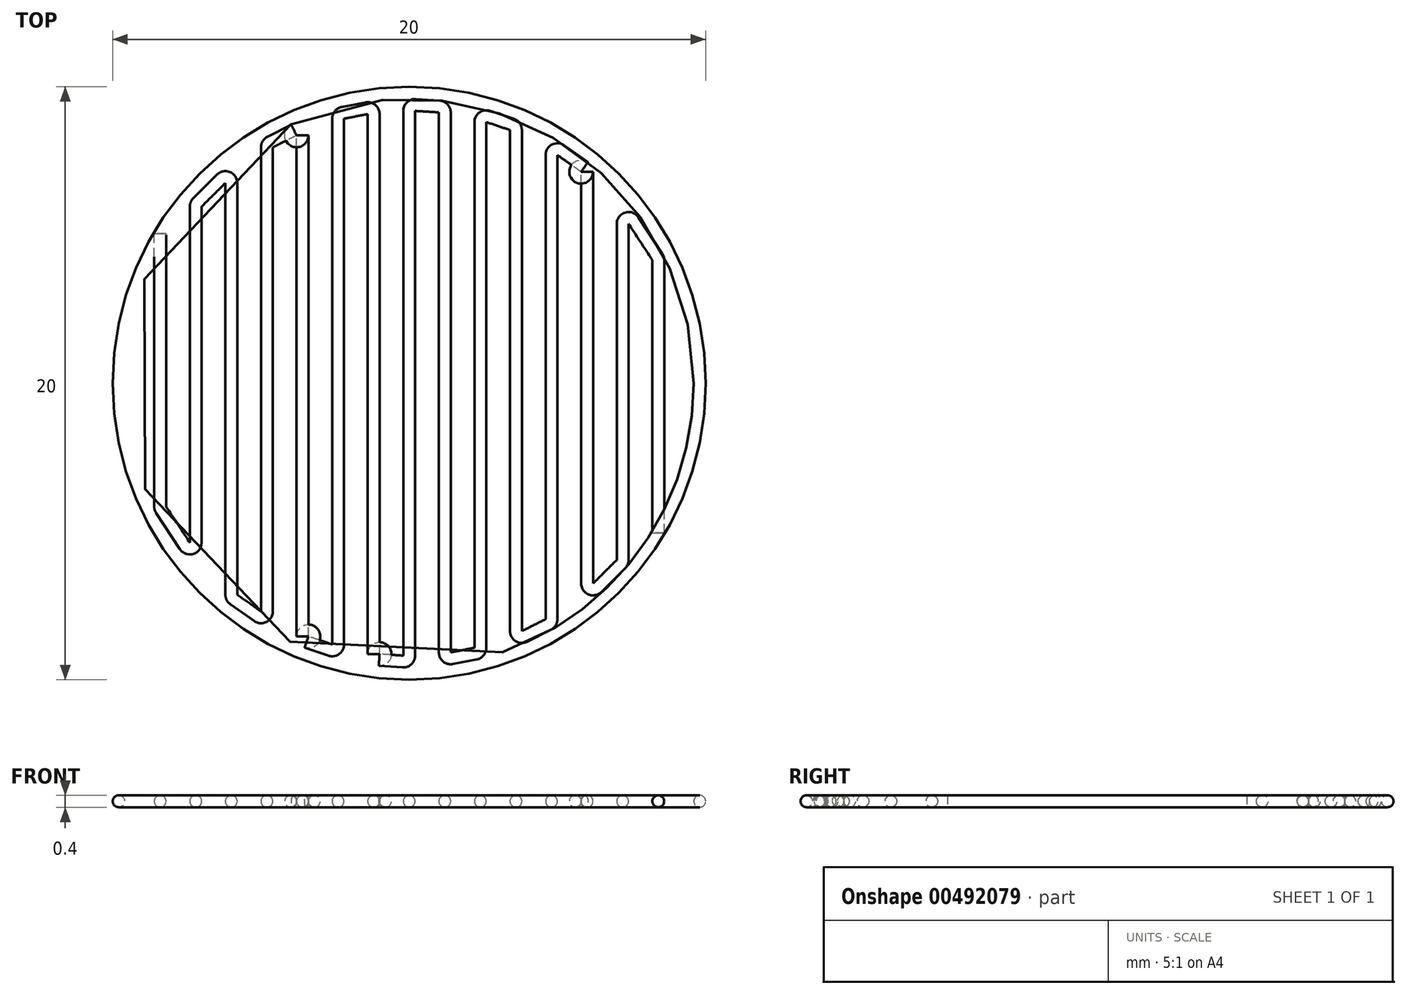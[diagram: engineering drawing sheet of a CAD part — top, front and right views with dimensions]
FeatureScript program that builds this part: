
annotation { "Feature Type Name" : "Feature", "Feature Type Description" : "" }
export const myFeature = defineFeature(function(context is Context, id is Id, definition is map)
    precondition{}
    {
        {
            assignVariable(context, id + "F0", {"name" : "d", "anyValue" : 0.4 * mm});
        }
        {
            var Q0;
            Q0=qCreatedBy(makeId("Top.planeOp"),FACE);
            cPlane(context, id + "F1", {"entities" : qUnion([Q0]), "cplaneType" : CPlaneType.OFFSET, "offset" : getVariable(context, 'd') / 2, "width" : 150 * mm, "height" : 150 * mm});
        }
        {
            var Q0;
            Q0=qCreatedBy(id+"F1.planeOp",FACE);
            var sketch = newSketch(context, id + "F2", { "sketchPlane" : qUnion([Q0])});
            skLineSegment(sketch, "E0.bottom", {"start": v(10, 10) * mm, "end": v(-10, 10) * mm, "construction": true});
            skLineSegment(sketch, "E0.top", {"start": v(10, -10) * mm, "end": v(-10, -10) * mm, "construction": true});
            skLineSegment(sketch, "E0.left", {"start": v(10, 10) * mm, "end": v(10, -10) * mm, "construction": true});
            skLineSegment(sketch, "E0.right", {"start": v(-10, 10) * mm, "end": v(-10, -10) * mm, "construction": true});
            skPoint(sketch, "E0.middle", {"position": v(0, 0) * mm});
            skCircle(sketch, "E1", {"center": v(0, 0) * mm, "radius": 9.8 * mm});
            skCircle(sketch, "E2", {"center": v(0, 0) * mm, "radius": 9.4 * mm, "construction": true});
            skLineSegment(sketch, "E3", {"start": v(10, -10) * mm, "end": v(9.6, -10) * mm, "construction": true});
            skLineSegment(sketch, "E4", {"start": v(9.6, -10) * mm, "end": v(8.4, -10) * mm, "construction": true});
            skLineSegment(sketch, "E5", {"start": v(8.4, -10) * mm, "end": v(7.2, -10) * mm, "construction": true});
            skLineSegment(sketch, "E6", {"start": v(7.2, -10) * mm, "end": v(6, -10) * mm, "construction": true});
            skLineSegment(sketch, "E7", {"start": v(6, -10) * mm, "end": v(4.8, -10) * mm, "construction": true});
            skLineSegment(sketch, "E8", {"start": v(4.8, -10) * mm, "end": v(3.6, -10) * mm, "construction": true});
            skLineSegment(sketch, "E9", {"start": v(3.6, -10) * mm, "end": v(2.4, -10) * mm, "construction": true});
            skLineSegment(sketch, "E10", {"start": v(2.4, -10) * mm, "end": v(1.2, -10) * mm, "construction": true});
            skLineSegment(sketch, "E11", {"start": v(1.2, -10) * mm, "end": v(0, -10) * mm, "construction": true});
            skLineSegment(sketch, "E12", {"start": v(0, -10) * mm, "end": v(-1.2, -10) * mm, "construction": true});
            skLineSegment(sketch, "E13", {"start": v(-1.2, -10) * mm, "end": v(-2.4, -10) * mm, "construction": true});
            skLineSegment(sketch, "E14", {"start": v(-2.4, -10) * mm, "end": v(-3.6, -10) * mm, "construction": true});
            skLineSegment(sketch, "E15", {"start": v(-3.6, -10) * mm, "end": v(-4.8, -10) * mm, "construction": true});
            skLineSegment(sketch, "E16", {"start": v(-4.8, -10) * mm, "end": v(-6, -10) * mm, "construction": true});
            skLineSegment(sketch, "E17", {"start": v(-6, -10) * mm, "end": v(-10, -10) * mm, "construction": true});
            skLineSegment(sketch, "E18", {"start": v(-6, -10) * mm, "end": v(-7.2, -10) * mm, "construction": true});
            skLineSegment(sketch, "E19", {"start": v(-7.2, -10) * mm, "end": v(-8.4, -10) * mm, "construction": true});
            skLineSegment(sketch, "E20", {"start": v(-8.4, -10) * mm, "end": v(-9.6, -10) * mm, "construction": true});
            skLineSegment(sketch, "E21", {"start": v(-9.6, -10) * mm, "end": v(-10, -10) * mm, "construction": true});
            skLineSegment(sketch, "E22", {"start": v(9.6, -10) * mm, "end": v(9.6, 10) * mm, "construction": true});
            skLineSegment(sketch, "E23", {"start": v(9.6, 10) * mm, "end": v(10, 10) * mm, "construction": true});
            skLineSegment(sketch, "E24", {"start": v(-9.6, -10) * mm, "end": v(-9.6, 10) * mm, "construction": true});
            skLineSegment(sketch, "E25", {"start": v(-9.6, 10) * mm, "end": v(-10, 10) * mm, "construction": true});
            skLineSegment(sketch, "E26", {"start": v(7.2, -10) * mm, "end": v(7.2, -6.04) * mm, "construction": true});
            skLineSegment(sketch, "E27", {"start": v(7.2, -5.96) * mm, "end": v(7.2, 5.38) * mm});
            skLineSegment(sketch, "E28", {"start": v(7.2, 6.04) * mm, "end": v(7.2, 10) * mm, "construction": true});
            skLineSegment(sketch, "E29", {"start": v(6, -10) * mm, "end": v(6, -7.24) * mm, "construction": true});
            skLineSegment(sketch, "E30", {"start": v(6, -6.76) * mm, "end": v(6, 7.13) * mm});
            skLineSegment(sketch, "E31", {"start": v(6, 7.24) * mm, "end": v(6, 10) * mm, "construction": true});
            skLineSegment(sketch, "E32", {"start": v(6, 10) * mm, "end": v(7.2, 10) * mm, "construction": true});
            skLineSegment(sketch, "E33", {"start": v(4.8, -10) * mm, "end": v(4.8, -8.08) * mm, "construction": true});
            skLineSegment(sketch, "E34", {"start": v(4.8, -7.96) * mm, "end": v(4.8, 7.7) * mm});
            skLineSegment(sketch, "E35", {"start": v(4.8, 8.08) * mm, "end": v(4.8, 10) * mm, "construction": true});
            skLineSegment(sketch, "E36", {"start": v(4.8, 10) * mm, "end": v(6, 10) * mm, "construction": true});
            skLineSegment(sketch, "E37", {"start": v(3.6, -10) * mm, "end": v(3.6, -8.68) * mm, "construction": true});
            skLineSegment(sketch, "E38", {"start": v(3.6, -8.36) * mm, "end": v(3.6, 8.54) * mm});
            skLineSegment(sketch, "E39", {"start": v(3.6, 8.68) * mm, "end": v(3.6, 10) * mm, "construction": true});
            skLineSegment(sketch, "E40", {"start": v(3.6, 10) * mm, "end": v(4.8, 10) * mm, "construction": true});
            skLineSegment(sketch, "E41", {"start": v(2.4, -10) * mm, "end": v(2.4, -9.09) * mm, "construction": true});
            skLineSegment(sketch, "E42", {"start": v(2.4, -8.92) * mm, "end": v(2.4, 8.8) * mm});
            skLineSegment(sketch, "E43", {"start": v(2.4, 9.09) * mm, "end": v(2.4, 10) * mm, "construction": true});
            skLineSegment(sketch, "E44", {"start": v(2.4, 10) * mm, "end": v(3.6, 10) * mm, "construction": true});
            skLineSegment(sketch, "E45", {"start": v(1.2, -10) * mm, "end": v(1.2, -9.32) * mm, "construction": true});
            skLineSegment(sketch, "E46", {"start": v(1.2, -9.08) * mm, "end": v(1.2, 9.14) * mm});
            skLineSegment(sketch, "E47", {"start": v(1.2, 9.32) * mm, "end": v(1.2, 10) * mm, "construction": true});
            skLineSegment(sketch, "E48", {"start": v(1.2, 10) * mm, "end": v(2.4, 10) * mm, "construction": true});
            skLineSegment(sketch, "E49", {"start": v(0, -10) * mm, "end": v(0, -9.4) * mm, "construction": true});
            skLineSegment(sketch, "E50", {"start": v(0, -9.19) * mm, "end": v(0, 9.19) * mm});
            skLineSegment(sketch, "E51", {"start": v(0, 9.4) * mm, "end": v(0, 10) * mm, "construction": true});
            skLineSegment(sketch, "E52", {"start": v(0, 10) * mm, "end": v(1.2, 10) * mm, "construction": true});
            skLineSegment(sketch, "E53", {"start": v(-1.2, -10) * mm, "end": v(-1.2, -9.32) * mm, "construction": true});
            skLineSegment(sketch, "E54", {"start": v(-1.2, -9.14) * mm, "end": v(-1.2, 9.08) * mm});
            skLineSegment(sketch, "E55", {"start": v(-1.2, 9.32) * mm, "end": v(-1.2, 10) * mm, "construction": true});
            skLineSegment(sketch, "E56", {"start": v(-1.2, 10) * mm, "end": v(0, 10) * mm, "construction": true});
            skLineSegment(sketch, "E57", {"start": v(-2.4, -10) * mm, "end": v(-2.4, -9.09) * mm, "construction": true});
            skLineSegment(sketch, "E58", {"start": v(-2.4, -8.8) * mm, "end": v(-2.4, 8.92) * mm});
            skLineSegment(sketch, "E59", {"start": v(-2.4, 9.09) * mm, "end": v(-2.4, 10) * mm, "construction": true});
            skLineSegment(sketch, "E60", {"start": v(-2.4, 10) * mm, "end": v(-1.2, 10) * mm, "construction": true});
            skLineSegment(sketch, "E61", {"start": v(-3.6, -10) * mm, "end": v(-3.6, -8.68) * mm, "construction": true});
            skLineSegment(sketch, "E62", {"start": v(-3.6, -8.54) * mm, "end": v(-3.6, 8.36) * mm});
            skLineSegment(sketch, "E63", {"start": v(-3.6, 8.68) * mm, "end": v(-3.6, 10) * mm, "construction": true});
            skLineSegment(sketch, "E64", {"start": v(-3.6, 10) * mm, "end": v(-2.4, 10) * mm, "construction": true});
            skLineSegment(sketch, "E65", {"start": v(-4.8, -10) * mm, "end": v(-4.8, -8.08) * mm, "construction": true});
            skLineSegment(sketch, "E66", {"start": v(-4.8, -7.7) * mm, "end": v(-4.8, 7.96) * mm});
            skLineSegment(sketch, "E67", {"start": v(-4.8, 8.08) * mm, "end": v(-4.8, 10) * mm, "construction": true});
            skLineSegment(sketch, "E68", {"start": v(-4.8, 10) * mm, "end": v(-3.6, 10) * mm, "construction": true});
            skLineSegment(sketch, "E69", {"start": v(-6, -10) * mm, "end": v(-6, -7.24) * mm, "construction": true});
            skLineSegment(sketch, "E70", {"start": v(-6, -7.13) * mm, "end": v(-6, 6.76) * mm});
            skLineSegment(sketch, "E71", {"start": v(-6, 7.24) * mm, "end": v(-6, 10) * mm, "construction": true});
            skLineSegment(sketch, "E72", {"start": v(-6, 10) * mm, "end": v(-4.8, 10) * mm, "construction": true});
            skLineSegment(sketch, "E73", {"start": v(-7.2, -10) * mm, "end": v(-7.2, -6.04) * mm, "construction": true});
            skLineSegment(sketch, "E74", {"start": v(-7.2, -5.38) * mm, "end": v(-7.2, 5.96) * mm});
            skLineSegment(sketch, "E75", {"start": v(-7.2, 6.04) * mm, "end": v(-7.2, 10) * mm, "construction": true});
            skLineSegment(sketch, "E76", {"start": v(-7.2, 10) * mm, "end": v(-6, 10) * mm, "construction": true});
            skLineSegment(sketch, "E77", {"start": v(-8.4, -10) * mm, "end": v(-8.4, -4.22) * mm, "construction": true});
            skLineSegment(sketch, "E78", {"start": v(8.4, -10) * mm, "end": v(8.4, -5.05) * mm, "construction": true});
            skLineSegment(sketch, "E79", {"start": v(8.4, -5.05) * mm, "end": v(8.4, 4.16) * mm});
            skLineSegment(sketch, "E80", {"start": v(8.4, 4.22) * mm, "end": v(8.4, 10) * mm, "construction": true});
            skLineSegment(sketch, "E81", {"start": v(8.4, 10) * mm, "end": v(9.6, 10) * mm, "construction": true});
            skLineSegment(sketch, "E82", {"start": v(7.2, 10) * mm, "end": v(8.4, 10) * mm, "construction": true});
            skLineSegment(sketch, "E83", {"start": v(-8.4, -4.16) * mm, "end": v(-8.4, 5.05) * mm});
            skLineSegment(sketch, "E84", {"start": v(-8.4, 5.05) * mm, "end": v(-8.4, 10) * mm, "construction": true});
            skLineSegment(sketch, "E85", {"start": v(-8.4, 10) * mm, "end": v(-7.2, 10) * mm, "construction": true});
            skLineSegment(sketch, "E86", {"start": v(-8.4, 10) * mm, "end": v(-9.6, 10) * mm, "construction": true});
            skLineSegment(sketch, "E87", {"start": v(-8.4, -4.22) * mm, "end": v(-8.4, 4.22) * mm});
            skLineSegment(sketch, "E88", {"start": v(8.4, -4.22) * mm, "end": v(8.4, 4.22) * mm});
            skLineSegment(sketch, "E89", {"start": v(8.37, 4.27) * mm, "end": v(7.57, 5.49) * mm});
            skLineSegment(sketch, "E90", {"start": v(5.92, 7.3) * mm, "end": v(5.12, 7.86) * mm});
            skLineSegment(sketch, "E91", {"start": v(3.46, 8.73) * mm, "end": v(2.66, 9) * mm});
            skLineSegment(sketch, "E92", {"start": v(1.01, 9.34) * mm, "end": v(0.21, 9.39) * mm});
            skLineSegment(sketch, "E93", {"start": v(-1.44, 9.28) * mm, "end": v(-2.24, 9.12) * mm});
            skLineSegment(sketch, "E94", {"start": v(-3.89, 8.54) * mm, "end": v(-4.69, 8.14) * mm});
            skLineSegment(sketch, "E95", {"start": v(-6.34, 6.9) * mm, "end": v(-7.14, 6.1) * mm});
            skLineSegment(sketch, "E96", {"start": v(-8.37, -4.27) * mm, "end": v(-7.57, -5.49) * mm});
            skLineSegment(sketch, "E97", {"start": v(-5.92, -7.3) * mm, "end": v(-5.12, -7.86) * mm});
            skLineSegment(sketch, "E98", {"start": v(-3.46, -8.73) * mm, "end": v(-2.66, -9) * mm});
            skLineSegment(sketch, "E99", {"start": v(-1.01, -9.34) * mm, "end": v(-0.21, -9.39) * mm});
            skLineSegment(sketch, "E100", {"start": v(1.44, -9.28) * mm, "end": v(2.24, -9.12) * mm});
            skLineSegment(sketch, "E101", {"start": v(3.89, -8.54) * mm, "end": v(4.69, -8.14) * mm});
            skLineSegment(sketch, "E102", {"start": v(6.34, -6.9) * mm, "end": v(7.14, -6.1) * mm});
            skPoint(sketch, "E103.visualSharp", {"position": v(8.4, 4.22) * mm});
            skArc(sketch, "E103.filletArc", {"start": v(8.4, 4.16) * mm, "mid": v(8.4, 4.22) * mm, "end": v(8.37, 4.27) * mm});
            skPoint(sketch, "E104.visualSharp", {"position": v(7.2, 6.04) * mm});
            skArc(sketch, "E104.filletArc", {"start": v(7.57, 5.49) * mm, "mid": v(7.34, 5.57) * mm, "end": v(7.2, 5.38) * mm});
            skPoint(sketch, "E105.visualSharp", {"position": v(7.2, -6.04) * mm});
            skArc(sketch, "E105.filletArc", {"start": v(7.14, -6.1) * mm, "mid": v(7.18, -6.04) * mm, "end": v(7.2, -5.96) * mm});
            skPoint(sketch, "E106.visualSharp", {"position": v(6, -7.24) * mm});
            skArc(sketch, "E106.filletArc", {"start": v(6, -6.76) * mm, "mid": v(6.12, -6.94) * mm, "end": v(6.34, -6.9) * mm});
            skPoint(sketch, "E107.visualSharp", {"position": v(6, 7.24) * mm});
            skArc(sketch, "E107.filletArc", {"start": v(6, 7.13) * mm, "mid": v(5.98, 7.22) * mm, "end": v(5.92, 7.3) * mm});
            skPoint(sketch, "E108.visualSharp", {"position": v(4.8, 8.08) * mm});
            skArc(sketch, "E108.filletArc", {"start": v(5.12, 7.86) * mm, "mid": v(4.9, 7.87) * mm, "end": v(4.8, 7.7) * mm});
            skPoint(sketch, "E109.visualSharp", {"position": v(4.8, -8.08) * mm});
            skArc(sketch, "E109.filletArc", {"start": v(4.69, -8.14) * mm, "mid": v(4.77, -8.06) * mm, "end": v(4.8, -7.96) * mm});
            skPoint(sketch, "E110.visualSharp", {"position": v(3.6, -8.68) * mm});
            skArc(sketch, "E110.filletArc", {"start": v(3.6, -8.36) * mm, "mid": v(3.7, -8.53) * mm, "end": v(3.89, -8.54) * mm});
            skPoint(sketch, "E111.visualSharp", {"position": v(3.6, 8.68) * mm});
            skArc(sketch, "E111.filletArc", {"start": v(3.6, 8.54) * mm, "mid": v(3.56, 8.66) * mm, "end": v(3.46, 8.73) * mm});
            skPoint(sketch, "E112.visualSharp", {"position": v(1.2, -9.32) * mm});
            skArc(sketch, "E112.filletArc", {"start": v(1.2, -9.08) * mm, "mid": v(1.27, -9.23) * mm, "end": v(1.44, -9.28) * mm});
            skPoint(sketch, "E113.visualSharp", {"position": v(0, 9.4) * mm});
            skArc(sketch, "E113.filletArc", {"start": v(0.21, 9.39) * mm, "mid": v(0.06, 9.33) * mm, "end": v(0, 9.19) * mm});
            skPoint(sketch, "E114.visualSharp", {"position": v(1.2, 9.32) * mm});
            skArc(sketch, "E114.filletArc", {"start": v(1.2, 9.14) * mm, "mid": v(1.15, 9.27) * mm, "end": v(1.01, 9.34) * mm});
            skPoint(sketch, "E115.visualSharp", {"position": v(-1.2, 9.32) * mm});
            skArc(sketch, "E115.filletArc", {"start": v(-1.2, 9.08) * mm, "mid": v(-1.27, 9.23) * mm, "end": v(-1.44, 9.28) * mm});
            skPoint(sketch, "E116.visualSharp", {"position": v(-2.4, 9.09) * mm});
            skArc(sketch, "E116.filletArc", {"start": v(-2.24, 9.12) * mm, "mid": v(-2.35, 9.05) * mm, "end": v(-2.4, 8.92) * mm});
            skPoint(sketch, "E117.visualSharp", {"position": v(-3.6, 8.68) * mm});
            skArc(sketch, "E117.filletArc", {"start": v(-3.6, 8.36) * mm, "mid": v(-3.7, 8.53) * mm, "end": v(-3.89, 8.54) * mm});
            skPoint(sketch, "E118.visualSharp", {"position": v(-4.8, 8.08) * mm});
            skArc(sketch, "E118.filletArc", {"start": v(-4.69, 8.14) * mm, "mid": v(-4.77, 8.06) * mm, "end": v(-4.8, 7.96) * mm});
            skPoint(sketch, "E119.visualSharp", {"position": v(-6, 7.24) * mm});
            skArc(sketch, "E119.filletArc", {"start": v(-6, 6.76) * mm, "mid": v(-6.12, 6.94) * mm, "end": v(-6.34, 6.9) * mm});
            skPoint(sketch, "E120.visualSharp", {"position": v(-7.2, 6.04) * mm});
            skArc(sketch, "E120.filletArc", {"start": v(-7.14, 6.1) * mm, "mid": v(-7.18, 6.04) * mm, "end": v(-7.2, 5.96) * mm});
            skPoint(sketch, "E121.visualSharp", {"position": v(-8.4, -4.22) * mm});
            skArc(sketch, "E121.filletArc", {"start": v(-8.4, -4.16) * mm, "mid": v(-8.4, -4.22) * mm, "end": v(-8.37, -4.27) * mm});
            skPoint(sketch, "E122.visualSharp", {"position": v(-7.2, -6.04) * mm});
            skArc(sketch, "E122.filletArc", {"start": v(-7.57, -5.49) * mm, "mid": v(-7.34, -5.57) * mm, "end": v(-7.2, -5.38) * mm});
            skPoint(sketch, "E123.visualSharp", {"position": v(-6, -7.24) * mm});
            skArc(sketch, "E123.filletArc", {"start": v(-6, -7.13) * mm, "mid": v(-5.98, -7.22) * mm, "end": v(-5.92, -7.3) * mm});
            skPoint(sketch, "E124.visualSharp", {"position": v(-4.8, -8.08) * mm});
            skArc(sketch, "E124.filletArc", {"start": v(-5.12, -7.86) * mm, "mid": v(-4.9, -7.87) * mm, "end": v(-4.8, -7.7) * mm});
            skPoint(sketch, "E125.visualSharp", {"position": v(-3.6, -8.68) * mm});
            skArc(sketch, "E125.filletArc", {"start": v(-3.6, -8.54) * mm, "mid": v(-3.56, -8.66) * mm, "end": v(-3.46, -8.73) * mm});
            skPoint(sketch, "E126.visualSharp", {"position": v(-2.4, -9.09) * mm});
            skArc(sketch, "E126.filletArc", {"start": v(-2.66, -9) * mm, "mid": v(-2.48, -8.97) * mm, "end": v(-2.4, -8.8) * mm});
            skPoint(sketch, "E127.visualSharp", {"position": v(-1.2, -9.32) * mm});
            skArc(sketch, "E127.filletArc", {"start": v(-1.2, -9.14) * mm, "mid": v(-1.15, -9.27) * mm, "end": v(-1.01, -9.34) * mm});
            skPoint(sketch, "E128.visualSharp", {"position": v(0, -9.4) * mm});
            skArc(sketch, "E128.filletArc", {"start": v(-0.21, -9.39) * mm, "mid": v(-0.06, -9.33) * mm, "end": v(0, -9.19) * mm});
            skPoint(sketch, "E129.visualSharp", {"position": v(2.4, -9.09) * mm});
            skArc(sketch, "E129.filletArc", {"start": v(2.24, -9.12) * mm, "mid": v(2.35, -9.05) * mm, "end": v(2.4, -8.92) * mm});
            skPoint(sketch, "E130.visualSharp", {"position": v(2.4, 9.09) * mm});
            skArc(sketch, "E130.filletArc", {"start": v(2.66, 9) * mm, "mid": v(2.48, 8.97) * mm, "end": v(2.4, 8.8) * mm});
            skSolve(sketch);
        }
        {
            var Q0;
            Q0=sQuery(id+"F2.wireOp",EDGE,"E79");
            var Q1;
            Q1=sQuery(id+"F2.wireOp",VERTEX,"E78.end");
            cPlane(context, id + "F3", {"entities" : qUnion([Q0, Q1]), "cplaneType" : CPlaneType.LINE_POINT, "offset" : 25 * mm, "width" : 150 * mm, "height" : 150 * mm});
        }
        {
            var Q0;
            Q0=qCreatedBy(id+"F3.planeOp",FACE);
            var sketch = newSketch(context, id + "F4", { "sketchPlane" : qUnion([Q0])});
            skCircle(sketch, "E131", {"center": v(-8.4, 0.2) * mm, "radius": 0.2 * mm});
            skSolve(sketch);
        }
        {
            var Q0;
            Q0=makeQuery(id+"F4.imprint","IMPRINT",FACE,{"disambiguationData":[TD([[makeQuery(id+"F4.imprint","IMPRINT",EDGE,{"derivedFrom":sQuery(id+"F4.wireOp",EDGE,"E131")}),1.0]])]});
            var Q1;
            Q1=sQuery(id+"F2.wireOp",EDGE,"E79");
            var Q2;
            Q2=sQuery(id+"F2.wireOp",EDGE,"E89");
            var Q3;
            Q3=sQuery(id+"F2.wireOp",EDGE,"E103.filletArc");
            var Q4;
            Q4=sQuery(id+"F2.wireOp",EDGE,"E104.filletArc");
            var Q5;
            Q5=sQuery(id+"F2.wireOp",EDGE,"E27");
            var Q6;
            Q6=sQuery(id+"F2.wireOp",EDGE,"E105.filletArc");
            var Q7;
            Q7=sQuery(id+"F2.wireOp",EDGE,"E102");
            var Q8;
            Q8=sQuery(id+"F2.wireOp",EDGE,"E106.filletArc");
            var Q9;
            Q9=sQuery(id+"F2.wireOp",EDGE,"E30");
            var Q10;
            Q10=sQuery(id+"F2.wireOp",EDGE,"E90");
            var Q11;
            Q11=sQuery(id+"F2.wireOp",EDGE,"E108.filletArc");
            var Q12;
            Q12=sQuery(id+"F2.wireOp",EDGE,"E34");
            var Q13;
            Q13=sQuery(id+"F2.wireOp",EDGE,"E107.filletArc");
            var Q14;
            Q14=sQuery(id+"F2.wireOp",EDGE,"E109.filletArc");
            var Q15;
            Q15=sQuery(id+"F2.wireOp",EDGE,"E101");
            var Q16;
            Q16=sQuery(id+"F2.wireOp",EDGE,"E110.filletArc");
            var Q17;
            Q17=sQuery(id+"F2.wireOp",EDGE,"E38");
            var Q18;
            Q18=sQuery(id+"F2.wireOp",EDGE,"E111.filletArc");
            var Q19;
            Q19=sQuery(id+"F2.wireOp",EDGE,"E91");
            var Q20;
            Q20=sQuery(id+"F2.wireOp",EDGE,"E130.filletArc");
            var Q21;
            Q21=sQuery(id+"F2.wireOp",EDGE,"E42");
            var Q22;
            Q22=sQuery(id+"F2.wireOp",EDGE,"E129.filletArc");
            var Q23;
            Q23=sQuery(id+"F2.wireOp",EDGE,"E100");
            var Q24;
            Q24=sQuery(id+"F2.wireOp",EDGE,"E112.filletArc");
            var Q25;
            Q25=sQuery(id+"F2.wireOp",EDGE,"E46");
            var Q26;
            Q26=sQuery(id+"F2.wireOp",EDGE,"E114.filletArc");
            var Q27;
            Q27=sQuery(id+"F2.wireOp",EDGE,"E92");
            var Q28;
            Q28=sQuery(id+"F2.wireOp",EDGE,"E113.filletArc");
            var Q29;
            Q29=sQuery(id+"F2.wireOp",EDGE,"E50");
            var Q30;
            Q30=sQuery(id+"F2.wireOp",EDGE,"E126.filletArc");
            var Q31;
            Q31=sQuery(id+"F2.wireOp",EDGE,"E127.filletArc");
            var Q32;
            Q32=sQuery(id+"F2.wireOp",EDGE,"E128.filletArc");
            var Q33;
            Q33=sQuery(id+"F2.wireOp",EDGE,"E54");
            var Q34;
            Q34=sQuery(id+"F2.wireOp",EDGE,"E99");
            var Q35;
            Q35=sQuery(id+"F2.wireOp",EDGE,"E98");
            var Q36;
            Q36=sQuery(id+"F2.wireOp",EDGE,"E62");
            var Q37;
            Q37=sQuery(id+"F2.wireOp",EDGE,"E125.filletArc");
            var Q38;
            Q38=sQuery(id+"F2.wireOp",EDGE,"E58");
            var Q39;
            Q39=sQuery(id+"F2.wireOp",EDGE,"E66");
            var Q40;
            Q40=sQuery(id+"F2.wireOp",EDGE,"E124.filletArc");
            var Q41;
            Q41=sQuery(id+"F2.wireOp",EDGE,"E97");
            var Q42;
            Q42=sQuery(id+"F2.wireOp",EDGE,"E123.filletArc");
            var Q43;
            Q43=sQuery(id+"F2.wireOp",EDGE,"E70");
            var Q44;
            Q44=sQuery(id+"F2.wireOp",EDGE,"E74");
            var Q45;
            Q45=sQuery(id+"F2.wireOp",EDGE,"E122.filletArc");
            var Q46;
            Q46=sQuery(id+"F2.wireOp",EDGE,"E96");
            var Q47;
            Q47=sQuery(id+"F2.wireOp",EDGE,"E83");
            var Q48;
            Q48=sQuery(id+"F2.wireOp",EDGE,"E121.filletArc");
            var Q49;
            Q49=sQuery(id+"F2.wireOp",EDGE,"E95");
            var Q50;
            Q50=sQuery(id+"F2.wireOp",EDGE,"E120.filletArc");
            var Q51;
            Q51=sQuery(id+"F2.wireOp",EDGE,"E119.filletArc");
            var Q52;
            Q52=sQuery(id+"F2.wireOp",EDGE,"E118.filletArc");
            var Q53;
            Q53=sQuery(id+"F2.wireOp",EDGE,"E94");
            var Q54;
            Q54=sQuery(id+"F2.wireOp",EDGE,"E117.filletArc");
            var Q55;
            Q55=sQuery(id+"F2.wireOp",EDGE,"E116.filletArc");
            var Q56;
            Q56=sQuery(id+"F2.wireOp",EDGE,"E93");
            var Q57;
            Q57=sQuery(id+"F2.wireOp",EDGE,"E115.filletArc");
            sweep(context, id + "F5", {"profiles" : qUnion([Q0]), "path" : qUnion([Q1, Q2, Q3, Q4, Q5, Q6, Q7, Q8, Q9, Q10, Q11, Q12, Q13, Q14, Q15, Q16, Q17, Q18, Q19, Q20, Q21, Q22, Q23, Q24, Q25, Q26, Q27, Q28, Q29, Q30, Q31, Q32, Q33, Q34, Q35, Q36, Q37, Q38, Q39, Q40, Q41, Q42, Q43, Q44, Q45, Q46, Q47, Q48, Q49, Q50, Q51, Q52, Q53, Q54, Q55, Q56, Q57])});
        }
        {
            var Q0;
            Q0=qCreatedBy(makeId("Front.planeOp"),FACE);
            var sketch = newSketch(context, id + "F6", { "sketchPlane" : qUnion([Q0])});
            skCircle(sketch, "E132", {"center": v(9.8, 0.2) * mm, "radius": 0.2 * mm});
            skSolve(sketch);
        }
        {
            var Q0;
            Q0=qSketchRegion(id+"F6",true);
            var Q1;
            Q1=sQuery(id+"F2.wireOp",EDGE,"E1");
            sweep(context, id + "F7", {"profiles" : qUnion([Q0]), "path" : qUnion([Q1])});
        }
    });
